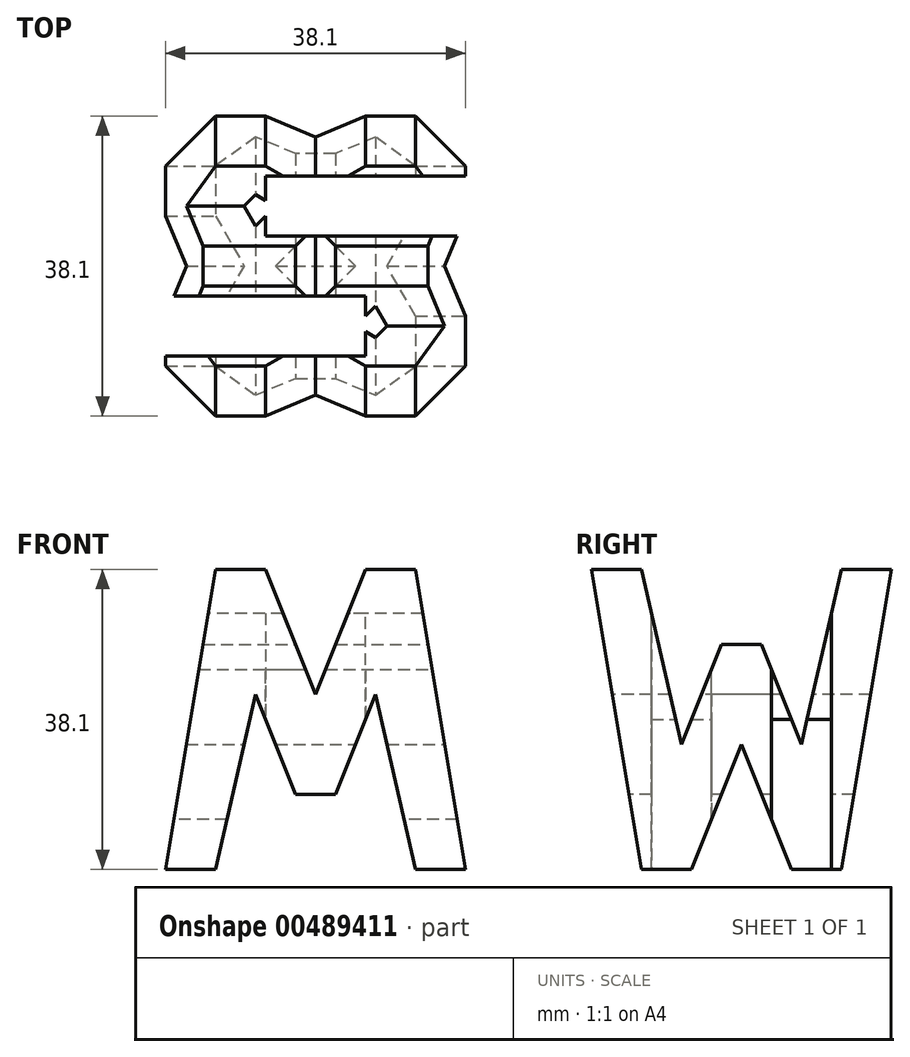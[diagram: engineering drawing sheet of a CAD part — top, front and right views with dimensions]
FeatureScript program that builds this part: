
annotation { "Feature Type Name" : "Feature", "Feature Type Description" : "" }
export const myFeature = defineFeature(function(context is Context, id is Id, definition is map)
    precondition{}
    {
        {
            var Q0;
            Q0=qCreatedBy(makeId("Front.planeOp"),FACE);
            var sketch = newSketch(context, id + "F0", { "sketchPlane" : qUnion([Q0])});
            skPoint(sketch, "E0.orphan", {"position": v(0, 38.1) * mm});
            skPoint(sketch, "E1.end.orphan", {"position": v(38.1, 0) * mm});
            skLineSegment(sketch, "E2", {"start": v(0, 38.1) * mm, "end": v(0, 0) * mm});
            skLineSegment(sketch, "E3", {"start": v(0, 0) * mm, "end": v(38.1, 0) * mm});
            skLineSegment(sketch, "E4", {"start": v(38.1, 38.1) * mm, "end": v(0, 38.1) * mm});
            skLineSegment(sketch, "E5", {"start": v(38.1, 38.1) * mm, "end": v(38.1, 0) * mm});
            skSolve(sketch);
        }
        {
            var Q0;
            Q0=makeQuery(id+"F0.imprint","IMPRINT",FACE,{"disambiguationData":[TD([[makeQuery(id+"F0.imprint","IMPRINT",EDGE,{"derivedFrom":sQuery(id+"F0.wireOp",EDGE,"E2")}),1.0]])]});
            extrude(context, id + "F1", {"entities" : qUnion([Q0]), "depth" : 38.1 * mm, "offsetDistance" : 25.4 * mm});
        }
        {
            var Q0;
            Q0=qCreatedBy(makeId("Front.planeOp"),FACE);
            cPlane(context, id + "F2", {"entities" : qUnion([Q0]), "cplaneType" : CPlaneType.OFFSET, "offset" : 38.1 * mm, "width" : 152.4 * mm, "height" : 152.4 * mm});
        }
        {
            var Q0;
            Q0=qCreatedBy(makeId("Right.planeOp"),FACE);
            cPlane(context, id + "F3", {"entities" : qUnion([Q0]), "cplaneType" : CPlaneType.OFFSET, "offset" : 38.1 * mm, "width" : 152.4 * mm, "height" : 152.4 * mm});
        }
        {
            var Q0;
            Q0=qCreatedBy(makeId("Top.planeOp"),FACE);
            cPlane(context, id + "F4", {"entities" : qUnion([Q0]), "cplaneType" : CPlaneType.OFFSET, "offset" : 38.1 * mm, "width" : 152.4 * mm, "height" : 152.4 * mm});
        }
        {
            var Q0;
            Q0=qCreatedBy(id+"F3.planeOp",FACE);
            var sketch = newSketch(context, id + "F5", { "sketchPlane" : qUnion([Q0])});
            skLineSegment(sketch, "E6", {"start": v(0, 0) * mm, "end": v(0, 38.1) * mm});
            skLineSegment(sketch, "E7", {"start": v(0, 38.1) * mm, "end": v(-38.1, 38.1) * mm});
            skLineSegment(sketch, "E8", {"start": v(-38.1, 38.1) * mm, "end": v(-38.1, 0) * mm});
            skLineSegment(sketch, "E9", {"start": v(-38.1, 0) * mm, "end": v(0, 0) * mm});
            skLineSegment(sketch, "E10", {"start": v(-38.1, 38.1) * mm, "end": v(-31.75, 0) * mm});
            skLineSegment(sketch, "E11", {"start": v(-25.4, 0) * mm, "end": v(-19.05, 15.88) * mm});
            skLineSegment(sketch, "E12", {"start": v(-19.05, 15.88) * mm, "end": v(-12.7, 0) * mm});
            skLineSegment(sketch, "E13", {"start": v(-6.35, 0) * mm, "end": v(0, 38.1) * mm});
            skLineSegment(sketch, "E14", {"start": v(-6.35, 38.1) * mm, "end": v(-11.43, 15.88) * mm});
            skLineSegment(sketch, "E15", {"start": v(-11.43, 15.88) * mm, "end": v(-16.5, 28.58) * mm});
            skLineSegment(sketch, "E16", {"start": v(-16.5, 28.58) * mm, "end": v(-21.59, 28.58) * mm});
            skLineSegment(sketch, "E17", {"start": v(-21.59, 28.58) * mm, "end": v(-26.67, 15.88) * mm});
            skLineSegment(sketch, "E18", {"start": v(-26.67, 15.88) * mm, "end": v(-31.75, 38.1) * mm});
            skPoint(sketch, "E19.end.orphan", {"position": v(-19.05, 0) * mm});
            skSolve(sketch);
        }
        {
            var Q0;
            {var subQ0=sQuery(id+"F5.wireOp",EDGE,"E8");Q0=makeQuery(id+"F5.imprint","IMPRINT",FACE,{"disambiguationData":[TD([[makeQuery(id+"F5.imprint","IMPRINT",EDGE,{"derivedFrom":subQ0}),1.0]])]});}
            var Q1;
            {var subQ0=sQuery(id+"F5.wireOp",EDGE,"E11");Q1=makeQuery(id+"F5.imprint","IMPRINT",FACE,{"disambiguationData":[TD([[makeQuery(id+"F5.imprint","IMPRINT",EDGE,{"derivedFrom":subQ0}),-1.0]])]});}
            var Q2;
            {var subQ0=sQuery(id+"F5.wireOp",EDGE,"E6");Q2=makeQuery(id+"F5.imprint","IMPRINT",FACE,{"disambiguationData":[TD([[makeQuery(id+"F5.imprint","IMPRINT",EDGE,{"derivedFrom":subQ0}),1.0]])]});}
            var Q3;
            {var subQ0=sQuery(id+"F5.wireOp",EDGE,"E14");Q3=makeQuery(id+"F5.imprint","IMPRINT",FACE,{"disambiguationData":[TD([[makeQuery(id+"F5.imprint","IMPRINT",EDGE,{"derivedFrom":subQ0}),-1.0]])]});}
            extrude(context, id + "F6", {"entities" : qUnion([Q0, Q1, Q2, Q3]), "operationType" : NewBodyOperationType.REMOVE, "oppositeDirection" : true, "depth" : 38.1 * mm, "offsetDistance" : 25.4 * mm});
        }
        {
            var Q0;
            Q0=qCreatedBy(id+"F2.planeOp",FACE);
            var sketch = newSketch(context, id + "F7", { "sketchPlane" : qUnion([Q0])});
            skLineSegment(sketch, "E20", {"start": v(0, 0) * mm, "end": v(0, 38.1) * mm});
            skLineSegment(sketch, "E21", {"start": v(0, 38.1) * mm, "end": v(38.1, 38.1) * mm});
            skLineSegment(sketch, "E22", {"start": v(38.1, 38.1) * mm, "end": v(38.1, 0) * mm});
            skLineSegment(sketch, "E23", {"start": v(38.1, 0) * mm, "end": v(0, 0) * mm});
            skLineSegment(sketch, "E24", {"start": v(6.35, 38.1) * mm, "end": v(0, 0) * mm});
            skLineSegment(sketch, "E25", {"start": v(12.7, 38.1) * mm, "end": v(19.05, 22.22) * mm});
            skLineSegment(sketch, "E26", {"start": v(19.05, 22.22) * mm, "end": v(25.4, 38.1) * mm});
            skLineSegment(sketch, "E27", {"start": v(31.75, 38.1) * mm, "end": v(38.1, 0) * mm});
            skLineSegment(sketch, "E28", {"start": v(6.35, 0) * mm, "end": v(11.43, 22.23) * mm});
            skLineSegment(sketch, "E29", {"start": v(11.43, 22.23) * mm, "end": v(16.51, 9.52) * mm});
            skLineSegment(sketch, "E30", {"start": v(16.51, 9.52) * mm, "end": v(21.6, 9.52) * mm});
            skLineSegment(sketch, "E31", {"start": v(21.6, 9.52) * mm, "end": v(26.67, 22.23) * mm});
            skLineSegment(sketch, "E32", {"start": v(26.67, 22.23) * mm, "end": v(31.75, 0) * mm});
            skSolve(sketch);
        }
        {
            var Q0;
            {var subQ0=sQuery(id+"F7.wireOp",EDGE,"E20");Q0=makeQuery(id+"F7.imprint","IMPRINT",FACE,{"disambiguationData":[TD([[makeQuery(id+"F7.imprint","IMPRINT",EDGE,{"derivedFrom":subQ0}),-1.0]])]});}
            var Q1;
            {var subQ0=sQuery(id+"F7.wireOp",EDGE,"E28");Q1=makeQuery(id+"F7.imprint","IMPRINT",FACE,{"disambiguationData":[TD([[makeQuery(id+"F7.imprint","IMPRINT",EDGE,{"derivedFrom":subQ0}),-1.0]])]});}
            var Q2;
            {var subQ0=sQuery(id+"F7.wireOp",EDGE,"E22");Q2=makeQuery(id+"F7.imprint","IMPRINT",FACE,{"disambiguationData":[TD([[makeQuery(id+"F7.imprint","IMPRINT",EDGE,{"derivedFrom":subQ0}),-1.0]])]});}
            var Q3;
            {var subQ0=sQuery(id+"F7.wireOp",EDGE,"E25");Q3=makeQuery(id+"F7.imprint","IMPRINT",FACE,{"disambiguationData":[TD([[makeQuery(id+"F7.imprint","IMPRINT",EDGE,{"derivedFrom":subQ0}),1.0]])]});}
            extrude(context, id + "F8", {"entities" : qUnion([Q0, Q1, Q2, Q3]), "operationType" : NewBodyOperationType.REMOVE, "oppositeDirection" : true, "depth" : 38.1 * mm, "offsetDistance" : 25.4 * mm});
        }
        {
            var Q0;
            Q0=qCreatedBy(id+"F4.planeOp",FACE);
            var sketch = newSketch(context, id + "F9", { "sketchPlane" : qUnion([Q0])});
            skLineSegment(sketch, "E33", {"start": v(0, 0) * mm, "end": v(0, -38.1) * mm});
            skLineSegment(sketch, "E34", {"start": v(0, -38.1) * mm, "end": v(38.1, -38.1) * mm});
            skLineSegment(sketch, "E35", {"start": v(38.1, -38.1) * mm, "end": v(38.1, 0) * mm});
            skLineSegment(sketch, "E36", {"start": v(38.1, 0) * mm, "end": v(0, 0) * mm});
            skLineSegment(sketch, "E37", {"start": v(38.1, -7.62) * mm, "end": v(12.7, -7.62) * mm});
            skLineSegment(sketch, "E38", {"start": v(12.7, -7.62) * mm, "end": v(12.7, -15.24) * mm});
            skLineSegment(sketch, "E39", {"start": v(12.7, -15.24) * mm, "end": v(38.1, -15.24) * mm});
            skLineSegment(sketch, "E40", {"start": v(0, -22.86) * mm, "end": v(25.4, -22.86) * mm});
            skLineSegment(sketch, "E41", {"start": v(25.4, -22.86) * mm, "end": v(25.4, -30.48) * mm});
            skLineSegment(sketch, "E42", {"start": v(25.4, -30.48) * mm, "end": v(0, -30.48) * mm});
            skSolve(sketch);
        }
        {
            var Q0;
            {var subQ0=sQuery(id+"F9.wireOp",EDGE,"E37");Q0=makeQuery(id+"F9.imprint","IMPRINT",FACE,{"disambiguationData":[TD([[makeQuery(id+"F9.imprint","IMPRINT",EDGE,{"derivedFrom":subQ0}),1.0]])]});}
            var Q1;
            {var subQ0=sQuery(id+"F9.wireOp",EDGE,"E40");Q1=makeQuery(id+"F9.imprint","IMPRINT",FACE,{"disambiguationData":[TD([[makeQuery(id+"F9.imprint","IMPRINT",EDGE,{"derivedFrom":subQ0}),-1.0]])]});}
            extrude(context, id + "F10", {"entities" : qUnion([Q0, Q1]), "operationType" : NewBodyOperationType.REMOVE, "oppositeDirection" : true, "depth" : 38.1 * mm, "offsetDistance" : 25.4 * mm});
        }
    });
